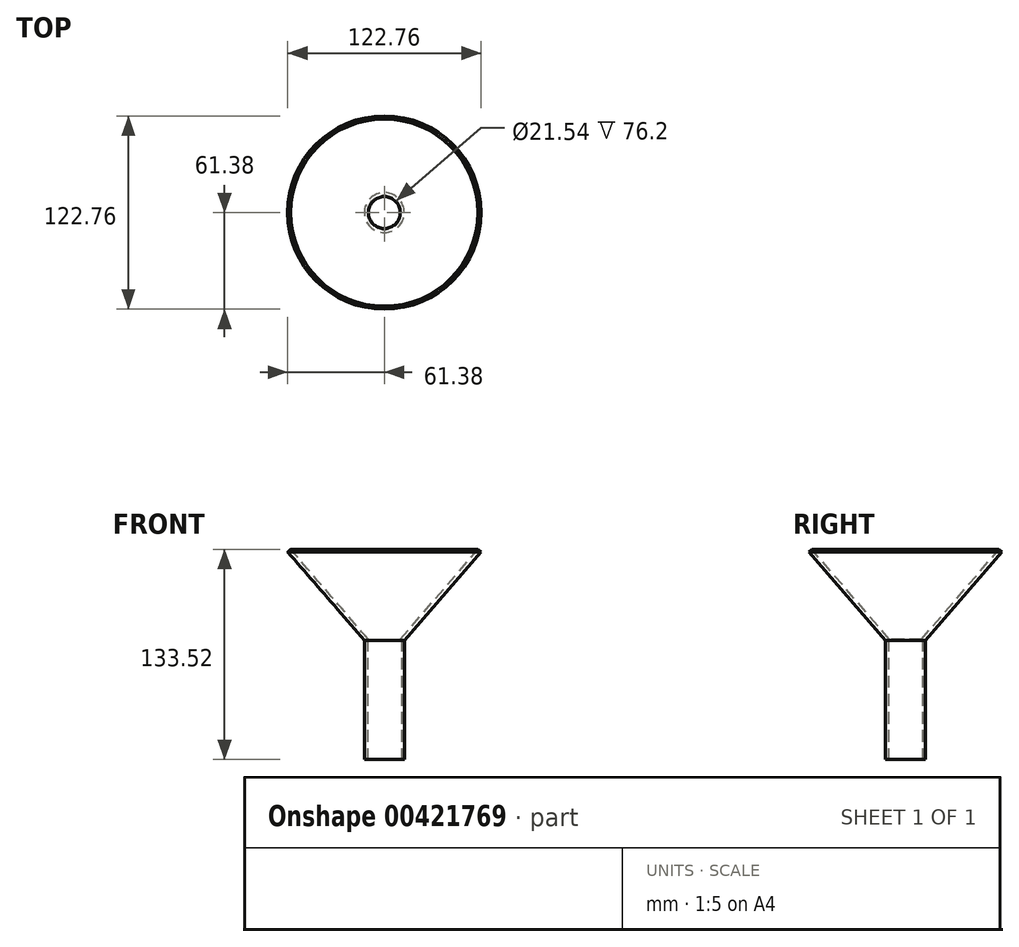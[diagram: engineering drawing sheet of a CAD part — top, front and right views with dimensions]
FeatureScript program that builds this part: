
annotation { "Feature Type Name" : "Feature", "Feature Type Description" : "" }
export const myFeature = defineFeature(function(context is Context, id is Id, definition is map)
    precondition{}
    {
        {
            var Q0;
            Q0=qCreatedBy(makeId("Front.planeOp"),FACE);
            var sketch = newSketch(context, id + "F0", { "sketchPlane" : qUnion([Q0])});
            skLineSegment(sketch, "E0", {"start": v(0, 0) * mm, "end": v(0, -75.78) * mm});
            skLineSegment(sketch, "E1", {"start": v(0, -75.78) * mm, "end": v(-12.7, -75.78) * mm});
            skLineSegment(sketch, "E2", {"start": v(-12.7, -75.78) * mm, "end": v(-12.7, 0) * mm});
            skLineSegment(sketch, "E3", {"start": v(-12.7, 0) * mm, "end": v(-2.97, 0) * mm});
            skLineSegment(sketch, "E4", {"start": v(-2.97, 0) * mm, "end": v(46.76, 57.74) * mm});
            skLineSegment(sketch, "E5", {"start": v(46.76, 57.74) * mm, "end": v(48.68, 56.08) * mm});
            skLineSegment(sketch, "E6", {"start": v(48.68, 56.08) * mm, "end": v(0, 0) * mm});
            skSolve(sketch);
        }
        {
            var Q0;
            Q0=makeQuery(id+"F0.imprint","IMPRINT",FACE,{"disambiguationData":[TD([[makeQuery(id+"F0.imprint","IMPRINT",EDGE,{"derivedFrom":sQuery(id+"F0.wireOp",EDGE,"E0")}),-1.0]])]});
            var Q1;
            Q1=sQuery(id+"F0.wireOp",EDGE,"E2");
            revolve(context, id + "F1", {"entities" : qUnion([Q0]), "axis" : qUnion([Q1]), "revolveType" : RevolveType.FULL});
        }
        {
            var Q0;
            Q0=makeQuery(id+"F1.opRevolve","SWEPT_FACE",FACE,{"disambiguationData":[OSD([sQuery(id+"F0.wireOp",EDGE,"E1")])]});
            var sketch = newSketch(context, id + "F2", { "sketchPlane" : qUnion([Q0])});
            skCircle(sketch, "E7", {"center": v(-12.7, 0) * mm, "radius": 10.77 * mm});
            skSolve(sketch);
        }
        {
            var Q0;
            Q0=makeQuery(id+"F2.imprint","IMPRINT",FACE,{"disambiguationData":[TD([[makeQuery(id+"F2.imprint","IMPRINT",EDGE,{"derivedFrom":sQuery(id+"F2.wireOp",EDGE,"E7")}),1.0]])]});
            extrude(context, id + "F3", {"entities" : qUnion([Q0]), "operationType" : NewBodyOperationType.REMOVE, "oppositeDirection" : true, "depth" : 25.4 * mm});
        }
        {
            var Q0;
            Q0=makeQuery(id+"F3.boolean.opBoolean","COPY",FACE,{"derivedFrom":makeQuery(id+"F3.opExtrude","CAP_FACE",FACE,{"disambiguationData":[OSD([sQuery(id+"F2.wireOp",EDGE,"E7")])],"isStart":false})});
            extrude(context, id + "F4", {"entities" : qUnion([Q0]), "operationType" : NewBodyOperationType.REMOVE, "oppositeDirection" : true, "depth" : 25.4 * mm});
        }
        {
            var Q0;
            Q0=makeQuery(id+"F4.boolean.opBoolean","COPY",FACE,{"derivedFrom":makeQuery(id+"F4.opExtrude","CAP_FACE",FACE,{"disambiguationData":[OSD([sQuery(id+"F2.wireOp",EDGE,"E7")])],"isStart":false})});
            extrude(context, id + "F5", {"entities" : qUnion([Q0]), "operationType" : NewBodyOperationType.REMOVE, "oppositeDirection" : true, "depth" : 25.4 * mm});
        }
    });
